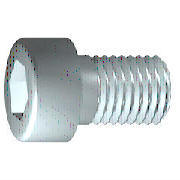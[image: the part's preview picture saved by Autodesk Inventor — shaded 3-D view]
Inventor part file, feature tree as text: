
AUTODESK INVENTOR PART (.ipt)
format: ipt  version: 2014 (Build 180170000, 170)  size: 192,000 bytes
history: native  units: mm (DEFAULTED — no unit token found)
features: sketch x2, extrude x1, plane x1, fillet x1
ambient origin geometry x7: Origin, YZ Plane, XY Plane, X Axis, Y Axis, Z Axis, Center Point
bodies: Solid1 (feature_tree), Body (feature_tree)
feature tree (5):
  extrude  "Slot"  Depth=2.5146mm
  plane  "Work Plane1"
  fillet  "Fillet2"  Radius=2.5146mm
  sketch  "Sketch1"  dims[d1=5.026968mm d2=1.322932mm d3=2.5146mm]
  sketch  "Sketch2"  dims[d4=1.1176mm d5=60.0deg d6=2.5146mm d7=2.5146mm d8=2.287693mm d9=4.0894mm d10=90.0deg d11=10.0mm d12=0.0mm d13=5.026968mm d14=0.0mm d15=0.31623mm d16=0.31623mm d17=0.2032mm d19=0.0mm d26=6.35mm d27=45.0deg d28=0.0mm d29=0.0mm d30=0.1016mm]
